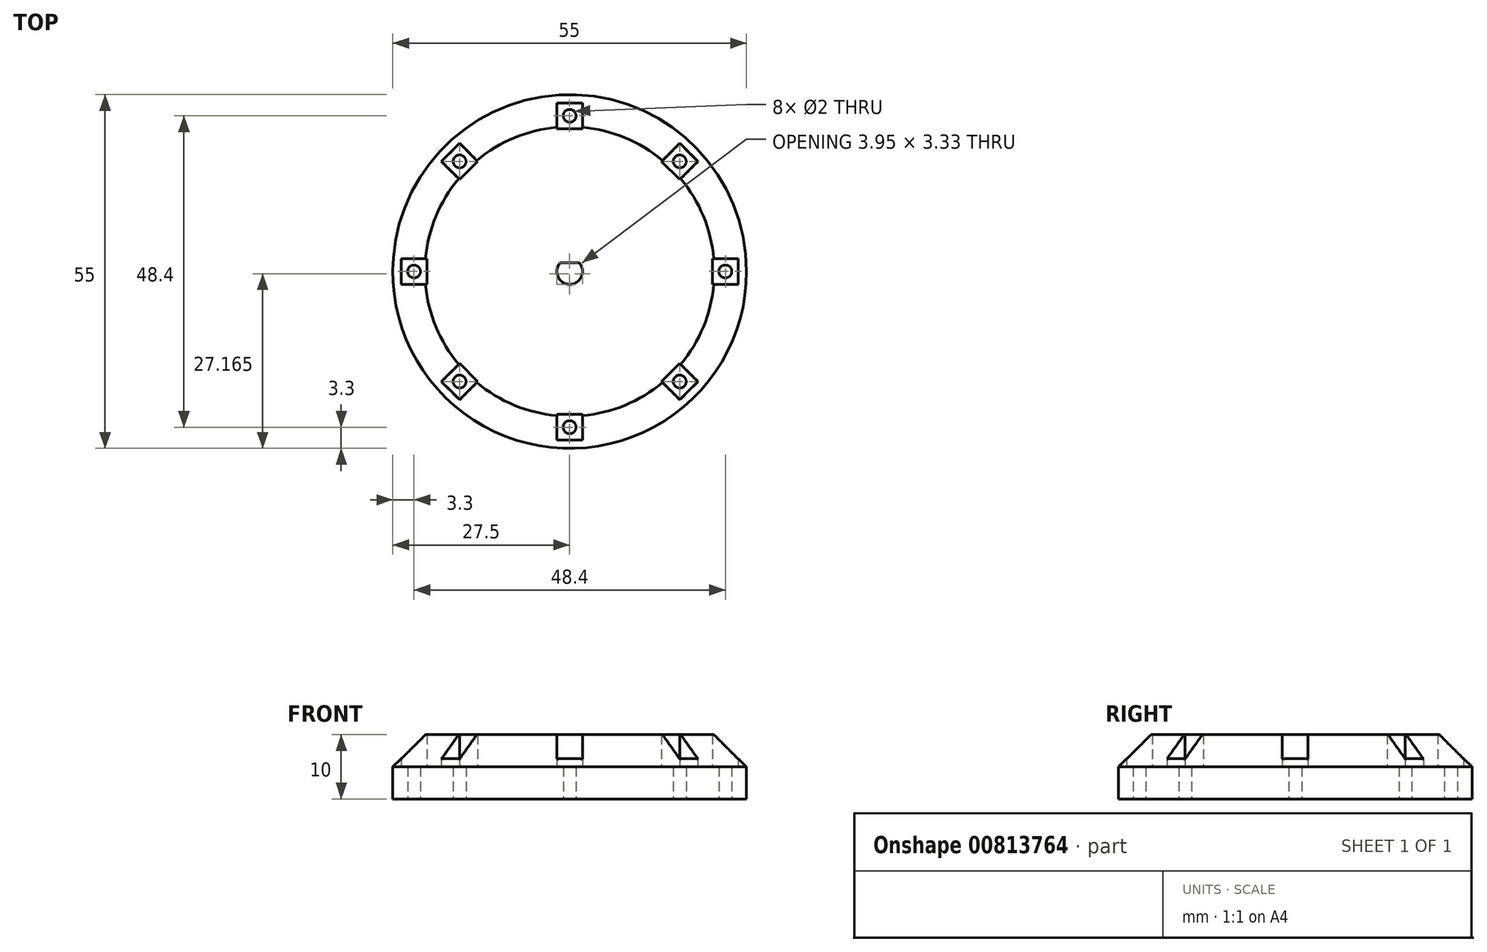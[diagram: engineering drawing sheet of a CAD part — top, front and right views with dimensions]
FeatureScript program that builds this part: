
annotation { "Feature Type Name" : "Feature", "Feature Type Description" : "" }
export const myFeature = defineFeature(function(context is Context, id is Id, definition is map)
    precondition{}
    {
        {
            var Q0;
            Q0=qCreatedBy(makeId("Top.planeOp"),FACE);
            var sketch = newSketch(context, id + "F0", { "sketchPlane" : qUnion([Q0])});
            skCircle(sketch, "E0", {"center": v(0, 0) * mm, "radius": 27.5 * mm});
            skCircle(sketch, "E1.0", {"center": v(0, 0) * mm, "radius": 21.1 * mm});
            skCircle(sketch, "E2", {"center": v(0, 24.2) * mm, "radius": 1 * mm});
            skCircle(sketch, "E3.1.0", {"center": v(-17.11, 17.11) * mm, "radius": 1 * mm});
            skCircle(sketch, "E3.2.0", {"center": v(-24.2, 0) * mm, "radius": 1 * mm});
            skCircle(sketch, "E3.3.0", {"center": v(-17.11, -17.11) * mm, "radius": 1 * mm});
            skCircle(sketch, "E3.4.0", {"center": v(0, -24.2) * mm, "radius": 1 * mm});
            skCircle(sketch, "E3.5.0", {"center": v(17.11, -17.11) * mm, "radius": 1 * mm});
            skCircle(sketch, "E3.6.0", {"center": v(24.2, 0) * mm, "radius": 1 * mm});
            skCircle(sketch, "E3.7.0", {"center": v(17.11, 17.11) * mm, "radius": 1 * mm});
            skArc(sketch, "E4", {"start": v(-1.5, 1.33) * mm, "mid": v(0, -2) * mm, "end": v(1.5, 1.33) * mm});
            skLineSegment(sketch, "E5", {"start": v(-1.5, 1.33) * mm, "end": v(1.5, 1.33) * mm});
            skSolve(sketch);
        }
        {
            var Q0;
            Q0=makeQuery(id+"F0.imprint","IMPRINT",FACE,{"disambiguationData":[TD([[makeQuery(id+"F0.imprint","IMPRINT",EDGE,{"derivedFrom":sQuery(id+"F0.wireOp",EDGE,"E0")}),1.0]])]});
            var Q1;
            Q1=makeQuery(id+"F0.imprint","IMPRINT",FACE,{"disambiguationData":[TD([[makeQuery(id+"F0.imprint","IMPRINT",EDGE,{"derivedFrom":sQuery(id+"F0.wireOp",EDGE,"E1.0")}),1.0]])]});
            extrude(context, id + "F1", {"entities" : qUnion([Q0, Q1]), "depth" : 10 * mm, "offsetDistance" : 25 * mm});
        }
        {
            var Q0;
            Q0=makeQuery(id+"F1.opExtrude","CAP_EDGE",EDGE,{"disambiguationData":[OSD([sQuery(id+"F0.wireOp",EDGE,"E0")])],"isStart":false});
            chamfer(context, id + "F2", {"entities" : qUnion([Q0]), "width" : 5 * mm, "tangentPropagation" : true});
        }
        {
            var Q0;
            Q0=makeQuery(id+"F0.imprint","IMPRINT",FACE,{"disambiguationData":[TD([[makeQuery(id+"F0.imprint","IMPRINT",EDGE,{"derivedFrom":sQuery(id+"F0.wireOp",EDGE,"E4")}),1.0]])]});
            extrude(context, id + "F3", {"entities" : qUnion([Q0]), "operationType" : NewBodyOperationType.REMOVE, "depth" : 10 * mm, "offsetDistance" : 25 * mm});
        }
        {
            var Q0;
            Q0=qCreatedBy(makeId("Top.planeOp"),FACE);
            cPlane(context, id + "F4", {"entities" : qUnion([Q0]), "cplaneType" : CPlaneType.OFFSET, "offset" : 5 * mm, "width" : 150 * mm, "height" : 150 * mm});
        }
        {
            var Q0;
            Q0=qCreatedBy(id+"F4.planeOp",FACE);
            var sketch = newSketch(context, id + "F5", { "sketchPlane" : qUnion([Q0])});
            skCircle(sketch, "E6.0", {"center": v(0, 24.2) * mm, "radius": 1 * mm});
            skLineSegment(sketch, "E7.bottom", {"start": v(2, 26.2) * mm, "end": v(-2, 26.2) * mm});
            skLineSegment(sketch, "E7.top", {"start": v(2, 22.2) * mm, "end": v(-2, 22.2) * mm});
            skLineSegment(sketch, "E7.left", {"start": v(2, 26.2) * mm, "end": v(2, 22.2) * mm});
            skLineSegment(sketch, "E7.right", {"start": v(-2, 26.2) * mm, "end": v(-2, 22.2) * mm});
            skCircle(sketch, "E8.0", {"center": v(0, 0) * mm, "radius": 27.5 * mm});
            skLineSegment(sketch, "E9.1.0", {"start": v(-17.11, 19.94) * mm, "end": v(-19.94, 17.11) * mm});
            skLineSegment(sketch, "E9.1.1", {"start": v(-19.94, 17.11) * mm, "end": v(-17.11, 14.28) * mm});
            skLineSegment(sketch, "E9.1.2", {"start": v(-14.28, 17.11) * mm, "end": v(-17.11, 14.28) * mm});
            skLineSegment(sketch, "E9.1.3", {"start": v(-17.11, 19.94) * mm, "end": v(-14.28, 17.11) * mm});
            skLineSegment(sketch, "E9.2.0", {"start": v(-26.2, 2) * mm, "end": v(-26.2, -2) * mm});
            skLineSegment(sketch, "E9.2.1", {"start": v(-26.2, -2) * mm, "end": v(-22.2, -2) * mm});
            skLineSegment(sketch, "E9.2.2", {"start": v(-22.2, 2) * mm, "end": v(-22.2, -2) * mm});
            skLineSegment(sketch, "E9.2.3", {"start": v(-26.2, 2) * mm, "end": v(-22.2, 2) * mm});
            skLineSegment(sketch, "E9.3.0", {"start": v(-19.94, -17.11) * mm, "end": v(-17.11, -19.94) * mm});
            skLineSegment(sketch, "E9.3.1", {"start": v(-17.11, -19.94) * mm, "end": v(-14.28, -17.11) * mm});
            skLineSegment(sketch, "E9.3.2", {"start": v(-17.11, -14.28) * mm, "end": v(-14.28, -17.11) * mm});
            skLineSegment(sketch, "E9.3.3", {"start": v(-19.94, -17.11) * mm, "end": v(-17.11, -14.28) * mm});
            skLineSegment(sketch, "E9.4.0", {"start": v(-2, -26.2) * mm, "end": v(2, -26.2) * mm});
            skLineSegment(sketch, "E9.4.1", {"start": v(2, -26.2) * mm, "end": v(2, -22.2) * mm});
            skLineSegment(sketch, "E9.4.2", {"start": v(-2, -22.2) * mm, "end": v(2, -22.2) * mm});
            skLineSegment(sketch, "E9.4.3", {"start": v(-2, -26.2) * mm, "end": v(-2, -22.2) * mm});
            skLineSegment(sketch, "E9.5.0", {"start": v(17.11, -19.94) * mm, "end": v(19.94, -17.11) * mm});
            skLineSegment(sketch, "E9.5.1", {"start": v(19.94, -17.11) * mm, "end": v(17.11, -14.28) * mm});
            skLineSegment(sketch, "E9.5.2", {"start": v(14.28, -17.11) * mm, "end": v(17.11, -14.28) * mm});
            skLineSegment(sketch, "E9.5.3", {"start": v(17.11, -19.94) * mm, "end": v(14.28, -17.11) * mm});
            skLineSegment(sketch, "E9.6.0", {"start": v(26.2, -2) * mm, "end": v(26.2, 2) * mm});
            skLineSegment(sketch, "E9.6.1", {"start": v(26.2, 2) * mm, "end": v(22.2, 2) * mm});
            skLineSegment(sketch, "E9.6.2", {"start": v(22.2, -2) * mm, "end": v(22.2, 2) * mm});
            skLineSegment(sketch, "E9.6.3", {"start": v(26.2, -2) * mm, "end": v(22.2, -2) * mm});
            skLineSegment(sketch, "E9.7.0", {"start": v(19.94, 17.11) * mm, "end": v(17.11, 19.94) * mm});
            skLineSegment(sketch, "E9.7.1", {"start": v(17.11, 19.94) * mm, "end": v(14.28, 17.11) * mm});
            skLineSegment(sketch, "E9.7.2", {"start": v(17.11, 14.28) * mm, "end": v(14.28, 17.11) * mm});
            skLineSegment(sketch, "E9.7.3", {"start": v(19.94, 17.11) * mm, "end": v(17.11, 14.28) * mm});
            skSolve(sketch);
        }
        {
            var Q0;
            Q0=makeQuery(id+"F5.imprint","IMPRINT",FACE,{"disambiguationData":[TD([[makeQuery(id+"F5.imprint","IMPRINT",EDGE,{"derivedFrom":sQuery(id+"F5.wireOp",EDGE,"E6.0")}),-1.0]])]});
            var Q1;
            Q1=makeQuery(id+"F5.imprint","IMPRINT",FACE,{"disambiguationData":[TD([[makeQuery(id+"F5.imprint","IMPRINT",EDGE,{"derivedFrom":sQuery(id+"F5.wireOp",EDGE,"E6.0")}),1.0]])]});
            var Q2;
            Q2=makeQuery(id+"F5.imprint","IMPRINT",FACE,{"disambiguationData":[TD([[makeQuery(id+"F5.imprint","IMPRINT",EDGE,{"derivedFrom":sQuery(id+"F5.wireOp",EDGE,"E9.1.0")}),1.0]])]});
            var Q3;
            Q3=makeQuery(id+"F5.imprint","IMPRINT",FACE,{"disambiguationData":[TD([[makeQuery(id+"F5.imprint","IMPRINT",EDGE,{"derivedFrom":sQuery(id+"F5.wireOp",EDGE,"E9.7.0")}),1.0]])]});
            var Q4;
            Q4=makeQuery(id+"F5.imprint","IMPRINT",FACE,{"disambiguationData":[TD([[makeQuery(id+"F5.imprint","IMPRINT",EDGE,{"derivedFrom":sQuery(id+"F5.wireOp",EDGE,"E9.2.0")}),1.0]])]});
            var Q5;
            Q5=makeQuery(id+"F5.imprint","IMPRINT",FACE,{"disambiguationData":[TD([[makeQuery(id+"F5.imprint","IMPRINT",EDGE,{"derivedFrom":sQuery(id+"F5.wireOp",EDGE,"E9.3.0")}),1.0]])]});
            var Q6;
            Q6=makeQuery(id+"F5.imprint","IMPRINT",FACE,{"disambiguationData":[TD([[makeQuery(id+"F5.imprint","IMPRINT",EDGE,{"derivedFrom":sQuery(id+"F5.wireOp",EDGE,"E9.4.0")}),1.0]])]});
            var Q7;
            Q7=makeQuery(id+"F5.imprint","IMPRINT",FACE,{"disambiguationData":[TD([[makeQuery(id+"F5.imprint","IMPRINT",EDGE,{"derivedFrom":sQuery(id+"F5.wireOp",EDGE,"E9.5.0")}),1.0]])]});
            var Q8;
            Q8=makeQuery(id+"F5.imprint","IMPRINT",FACE,{"disambiguationData":[TD([[makeQuery(id+"F5.imprint","IMPRINT",EDGE,{"derivedFrom":sQuery(id+"F5.wireOp",EDGE,"E9.6.0")}),1.0]])]});
            extrude(context, id + "F6", {"entities" : qUnion([Q0, Q1, Q2, Q3, Q4, Q5, Q6, Q7, Q8]), "operationType" : NewBodyOperationType.REMOVE, "depth" : 5 * mm, "offsetDistance" : 25 * mm});
        }
    });
